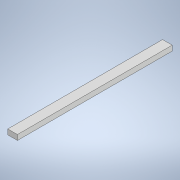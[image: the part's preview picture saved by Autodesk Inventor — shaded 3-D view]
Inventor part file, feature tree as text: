
AUTODESK INVENTOR PART (.ipt)
format: ipt  version: 2021 (Build 250183000, 183)  size: 92,672 bytes
history: native  units: in
note: dims shown in document units (in); Inventor stores cm internally (conversion verified against a paired STEP export)
features: extrude x1, sketch x1
ambient origin geometry x8: Origin, YZ Plane, XZ Plane, XY Plane, X Axis, Y Axis, Z Axis, Center Point
bodies: Solid1 (feature_tree)
feature tree (2):
  extrude  "Extrusion1"  Depth=0.2362in
  sketch  "Sketch1"  dims[d0=0.1252in d1=0.2362in d2=3.7795in d3=0.0in]
